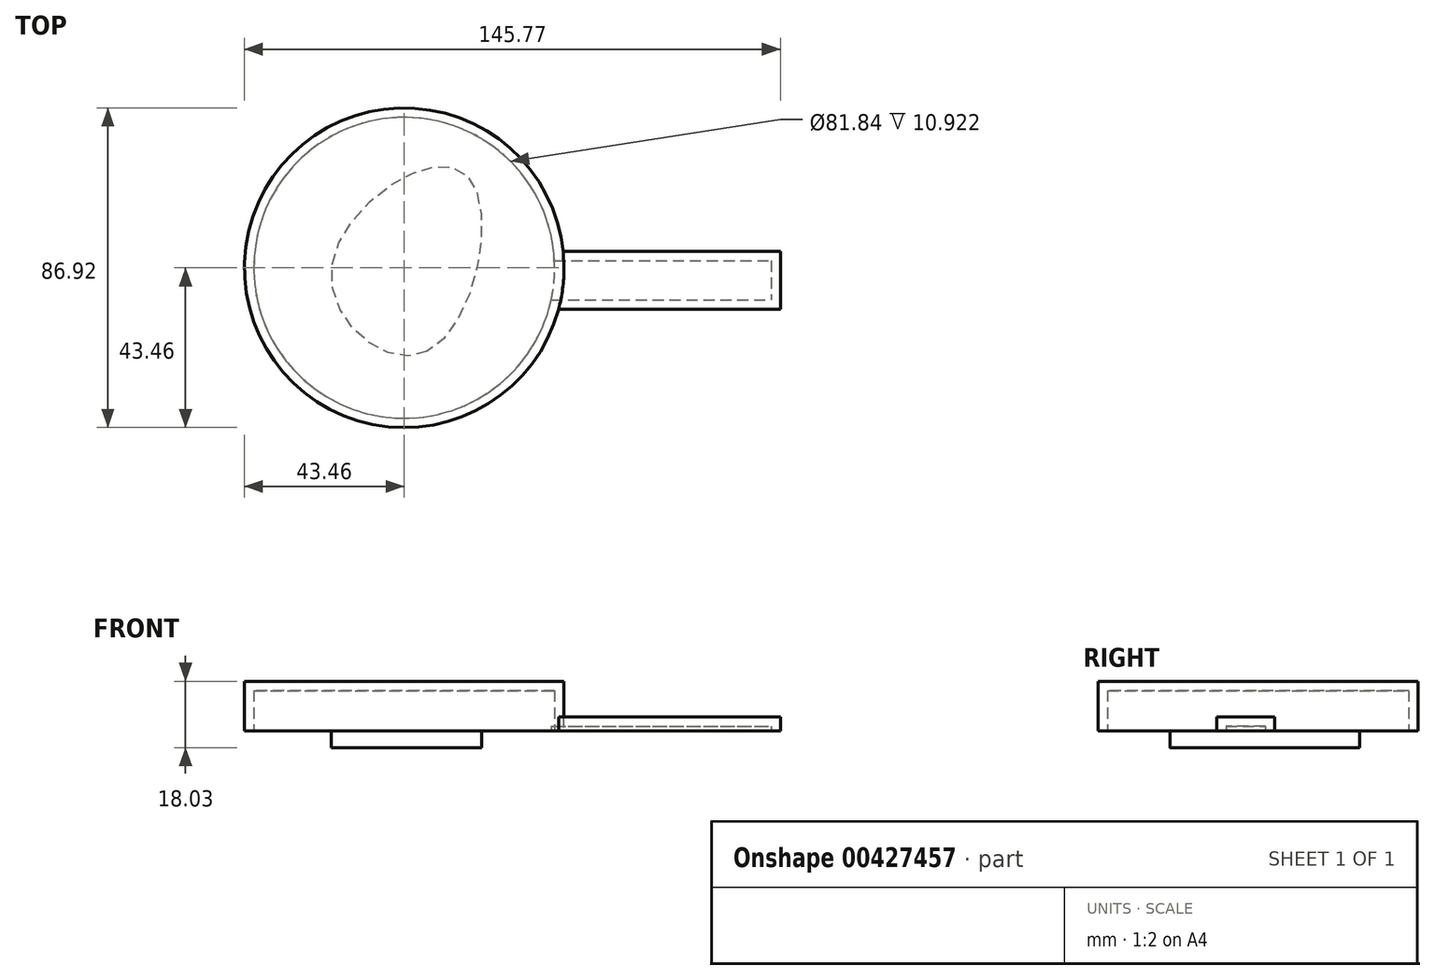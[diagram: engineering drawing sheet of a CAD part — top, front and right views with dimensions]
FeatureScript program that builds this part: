
annotation { "Feature Type Name" : "Feature", "Feature Type Description" : "" }
export const myFeature = defineFeature(function(context is Context, id is Id, definition is map)
    precondition{}
    {
        {
            var Q0;
            Q0=qCreatedBy(makeId("Top.planeOp"),FACE);
            var sketch = newSketch(context, id + "F0", { "sketchPlane" : qUnion([Q0])});
            skCircle(sketch, "E0", {"center": v(0, 0) * mm, "radius": 43.46 * mm});
            skLineSegment(sketch, "E1", {"start": v(43.23, 4.5) * mm, "end": v(102.3, 4.5) * mm});
            skLineSegment(sketch, "E2", {"start": v(41.96, -11.31) * mm, "end": v(102.3, -11.31) * mm});
            skLineSegment(sketch, "E3", {"start": v(102.3, 4.5) * mm, "end": v(102.3, -11.31) * mm});
            skSolve(sketch);
        }
        {
            var Q0;
            {var subQ0=sQuery(id+"F0.wireOp",EDGE,"E0");var subQ1=makeQuery(id+"F0.imprint","INTERSECT",VERTEX,{"derivedFrom":[subQ0,sQuery(id+"F0.wireOp",EDGE,"E1")]});Q0=makeQuery(id+"F0.imprint","IMPRINT",FACE,{"disambiguationData":[TD([[makeQuery(id+"F0.imprint","IMPRINT",EDGE,{"disambiguationData":[TD([[subQ1,-1.0]])],"derivedFrom":subQ0}),1.0]])]});}
            extrude(context, id + "F1", {"entities" : qUnion([Q0]), "depth" : 13.46 * mm});
        }
        {
            var Q0;
            {var subQ0=sQuery(id+"F0.wireOp",EDGE,"E1");Q0=makeQuery(id+"F0.imprint","IMPRINT",FACE,{"disambiguationData":[TD([[makeQuery(id+"F0.imprint","IMPRINT",EDGE,{"derivedFrom":subQ0}),-1.0]])]});}
            extrude(context, id + "F2", {"entities" : qUnion([Q0]), "operationType" : NewBodyOperationType.ADD, "depth" : 3.8 * mm});
        }
        {
            var Q0;
            {var subQ0=sQuery(id+"F0.wireOp",EDGE,"E0");Q0=makeQuery(id+"F2.boolean.opBoolean","MERGE",FACE,{"derivedFrom":[makeQuery(id+"F1.opExtrude","CAP_FACE",FACE,{"disambiguationData":[OSD([subQ0])],"isStart":true}),makeQuery(id+"F2.opExtrude","CAP_FACE",FACE,{"disambiguationData":[OSD([subQ0,sQuery(id+"F0.wireOp",EDGE,"E1"),sQuery(id+"F0.wireOp",EDGE,"E2"),sQuery(id+"F0.wireOp",EDGE,"E3")])],"isStart":true})]});}
            shell(context, id + "F3", {"entities" : qUnion([Q0]), "thickness" : 2.54 * mm});
        }
        {
            var Q0;
            Q0=qCreatedBy(makeId("Top.planeOp"),FACE);
            var sketch = newSketch(context, id + "F4", { "sketchPlane" : qUnion([Q0])});
            skFitSpline(sketch, "E4", {"points": [v(6.2, -22.74) * mm, v(-19.74, 0) * mm, v(16.11, 25.94) * mm, v(6.2, -22.74) * mm]});
            skSolve(sketch);
        }
        {
            var Q0;
            Q0=makeQuery(id+"F4.imprint","IMPRINT",FACE,{"disambiguationData":[TD([[makeQuery(id+"F4.imprint","IMPRINT",EDGE,{"derivedFrom":sQuery(id+"F4.wireOp",EDGE,"E4")}),-1.0]])]});
            extrude(context, id + "F5", {"entities" : qUnion([Q0]), "oppositeDirection" : true, "depth" : 4.57 * mm});
        }
    });
